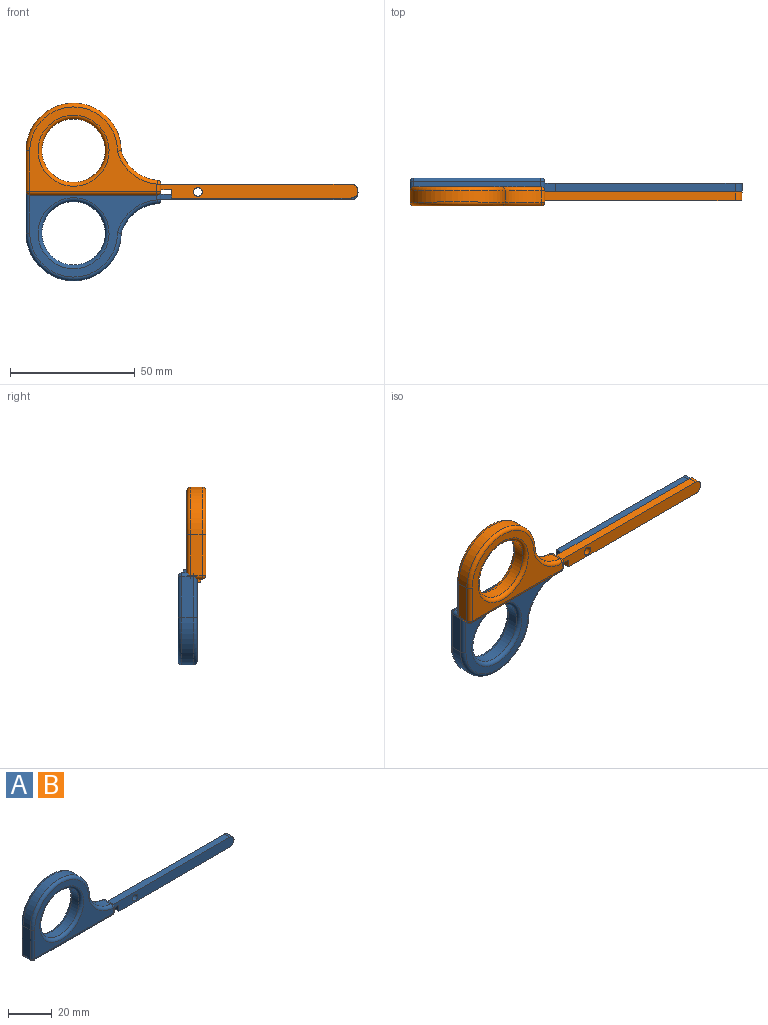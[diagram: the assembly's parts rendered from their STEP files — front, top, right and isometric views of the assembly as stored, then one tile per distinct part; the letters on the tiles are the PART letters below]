
ASSEMBLY  parts=2 mates=1
PART A: 37 faces, bbox 134.5x7.6x39.6 mm
  f0: plane 4.57x2.88mm, normal (1,0,0), area 5mm2, adj f1,f7,f15,f23,f29,f35,f36
  f1: cylinder r=1.52mm len=4.57mm, axis (0,1,0), area 10.4mm2, adj f0,f2,f17,f25,f34
  f2: cylinder r=16.51mm len=14.48mm, axis (0,1,0), area 91mm2, adj f1,f3,f18,f26
  f3: cylinder r=19.05mm len=38.1mm, axis (0,1,0), area 273.6mm2, adj f2,f4,f16,f24
  f4: plane 16.26x4.57mm, normal (-1,0,0), area 74.3mm2, adj f3,f5,f14,f22
  f5: cylinder r=1.52mm len=4.57mm, axis (0,1,0), area 10.9mm2, adj f4,f6,f12,f20
  f6: plane 50.93x4.57mm, normal (0,0,-1), area 232.8mm2, adj f5,f7,f11,f19
  f7: cylinder r=1.52mm len=4.57mm, axis (0,1,0), area 10.9mm2, adj f0,f6,f13,f21
  f8: cylinder r=12.7mm len=25.4mm, axis (0,1,0), area 364.8mm2, adj f27,f28
  f9: plane 50.93x33.78mm, normal (0,-1,0), area 521.5mm2, adj f19,f22,f23,f24,f26,f28
  f10: plane 50.93x33.78mm, normal (0,1,0), area 521.5mm2, adj f11,f14,f15,f16,f18,f27
  f11: cylinder r=1.52mm len=50.93mm, axis (1,0,0), area 121.9mm2, adj f6,f10,f12,f13
  f12: sphere r=1.52mm, area 3.6mm2, adj f5,f11,f14
  f13: sphere r=1.52mm, area 3.6mm2, adj f7,f11,f15
  f14: cylinder r=1.52mm len=16.26mm, axis (0,0,-1), area 38.9mm2, adj f4,f10,f12,f16
  f15: cylinder r=1.52mm len=2.88mm, axis (0,0,1), area 6.9mm2, adj f0,f10,f13,f17
  f16: torus R=17.53mm, axis (0,-1,0), area 139.3mm2, adj f3,f10,f14,f18
  f17: sphere r=1.52mm, area 3.5mm2, adj f1,f15,f18
  f18: torus R=18.03mm, axis (0,-1,0), area 49.4mm2, adj f2,f10,f16,f17
  f19: cylinder r=1.52mm len=50.93mm, axis (-1,0,0), area 121.9mm2, adj f6,f9,f20,f21
  f20: sphere r=1.52mm, area 3.6mm2, adj f5,f19,f22
  f21: sphere r=1.52mm, area 3.6mm2, adj f7,f19,f23
  f22: cylinder r=1.52mm len=16.26mm, axis (0,0,1), area 38.9mm2, adj f4,f9,f20,f24
  f23: cylinder r=1.52mm len=2.88mm, axis (0,0,-1), area 6.9mm2, adj f0,f9,f21,f25
  f24: torus R=17.53mm, axis (0,-1,0), area 139.3mm2, adj f3,f9,f22,f26
  f25: sphere r=1.52mm, area 3.5mm2, adj f1,f23,f26
  f26: torus R=18.03mm, axis (0,-1,0), area 49.4mm2, adj f2,f9,f24,f25
  f27: torus R=14.22mm, axis (0,-1,0), area 199.4mm2, adj f8,f10
  f28: torus R=14.22mm, axis (0,-1,0), area 199.4mm2, adj f8,f9
  f29: plane 4.32x3.56mm, normal (0,0,-1), area 15.4mm2, adj f0,f30,f35,f36
  f30: plane 3.56x3.3mm, normal (-1,0,0), area 11.7mm2, adj f29,f31,f35,f36
  f31: plane 71.88x3.56mm, normal (0,0,-1), area 255.6mm2, adj f30,f32,f35,f36
  f32: cylinder r=2.79mm len=5.59mm, axis (0,1,0), area 31.2mm2, adj f31,f34,f35,f36
  f33: cylinder r=1.71mm len=3.56mm, axis (0,1,0), area 38.3mm2, adj f35,f36
  f34: plane 76.2x3.56mm, normal (0,0,1), area 271mm2, adj f1,f32,f35,f36
  f35: plane 78.99x5.59mm, normal (0,-1,0), area 414.6mm2, adj f0,f29,f30,f31,f32,f33,f34
  f36: plane 78.99x5.59mm, normal (0,1,0), area 414.6mm2, adj f0,f29,f30,f31,f32,f33,f34
PART B: same geometry as A
PLACE A rot(axis=(1,0,0),180deg) t=(-21.29,18.85,4.08)mm
PLACE B t=(-21.29,15.3,19.39)mm
MATE revolute A.f33 <-> B.f33  axis (0,-1,0) through (-6.43,17.08,11.73)mm
